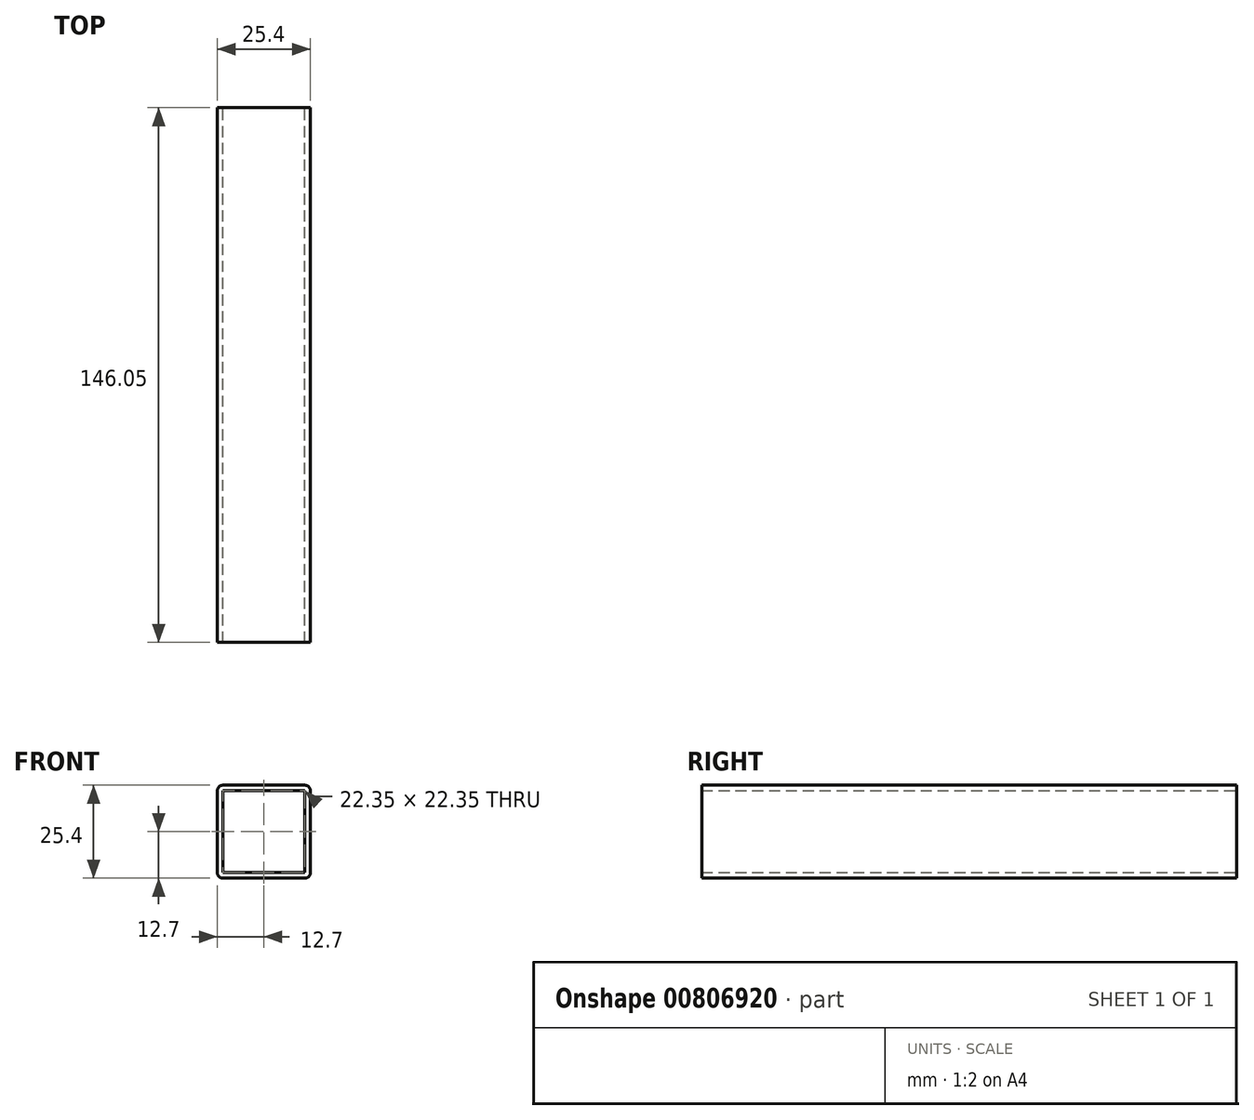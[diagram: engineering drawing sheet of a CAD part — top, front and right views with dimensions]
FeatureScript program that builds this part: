
annotation { "Feature Type Name" : "Feature", "Feature Type Description" : "" }
export const myFeature = defineFeature(function(context is Context, id is Id, definition is map)
    precondition{}
    {
        {
            var Q0;
            Q0=qCreatedBy(makeId("Front.planeOp"),FACE);
            var sketch = newSketch(context, id + "F0", { "sketchPlane" : qUnion([Q0])});
            skLineSegment(sketch, "E0.bottom", {"start": v(1.52, 0) * mm, "end": v(23.88, 0) * mm});
            skLineSegment(sketch, "E0.top", {"start": v(1.52, 25.4) * mm, "end": v(23.88, 25.4) * mm});
            skLineSegment(sketch, "E0.left", {"start": v(0, 1.52) * mm, "end": v(0, 23.88) * mm});
            skLineSegment(sketch, "E0.right", {"start": v(25.4, 1.52) * mm, "end": v(25.4, 23.88) * mm});
            skPoint(sketch, "E1.visualSharp", {"position": v(0, 25.4) * mm});
            skArc(sketch, "E1.filletArc", {"start": v(1.52, 25.4) * mm, "mid": v(0.45, 24.95) * mm, "end": v(0, 23.88) * mm});
            skPoint(sketch, "E2.visualSharp", {"position": v(25.4, 25.4) * mm});
            skArc(sketch, "E2.filletArc", {"start": v(25.4, 23.88) * mm, "mid": v(24.95, 24.95) * mm, "end": v(23.88, 25.4) * mm});
            skPoint(sketch, "E3.visualSharp", {"position": v(25.4, 0) * mm});
            skArc(sketch, "E3.filletArc", {"start": v(23.88, 0) * mm, "mid": v(24.95, 0.45) * mm, "end": v(25.4, 1.52) * mm});
            skPoint(sketch, "E4.visualSharp", {"position": v(0, 0) * mm});
            skArc(sketch, "E4.filletArc", {"start": v(0, 1.52) * mm, "mid": v(0.45, 0.45) * mm, "end": v(1.52, 0) * mm});
            skLineSegment(sketch, "E5.0", {"start": v(23.88, 1.52) * mm, "end": v(23.88, 23.88) * mm});
            skLineSegment(sketch, "E5.1", {"start": v(1.52, 1.52) * mm, "end": v(23.88, 1.52) * mm});
            skLineSegment(sketch, "E5.2", {"start": v(1.52, 1.52) * mm, "end": v(1.52, 23.88) * mm});
            skLineSegment(sketch, "E5.3", {"start": v(1.52, 23.88) * mm, "end": v(23.88, 23.88) * mm});
            skSolve(sketch);
        }
        {
            var Q0;
            Q0 = qSketchRegion(id + "F0", true);
            extrude(context, id + "F1", {"entities" : qUnion([Q0]), "depth" : 146.05 * mm, "offsetDistance" : 25.4 * mm});
        }
    });
